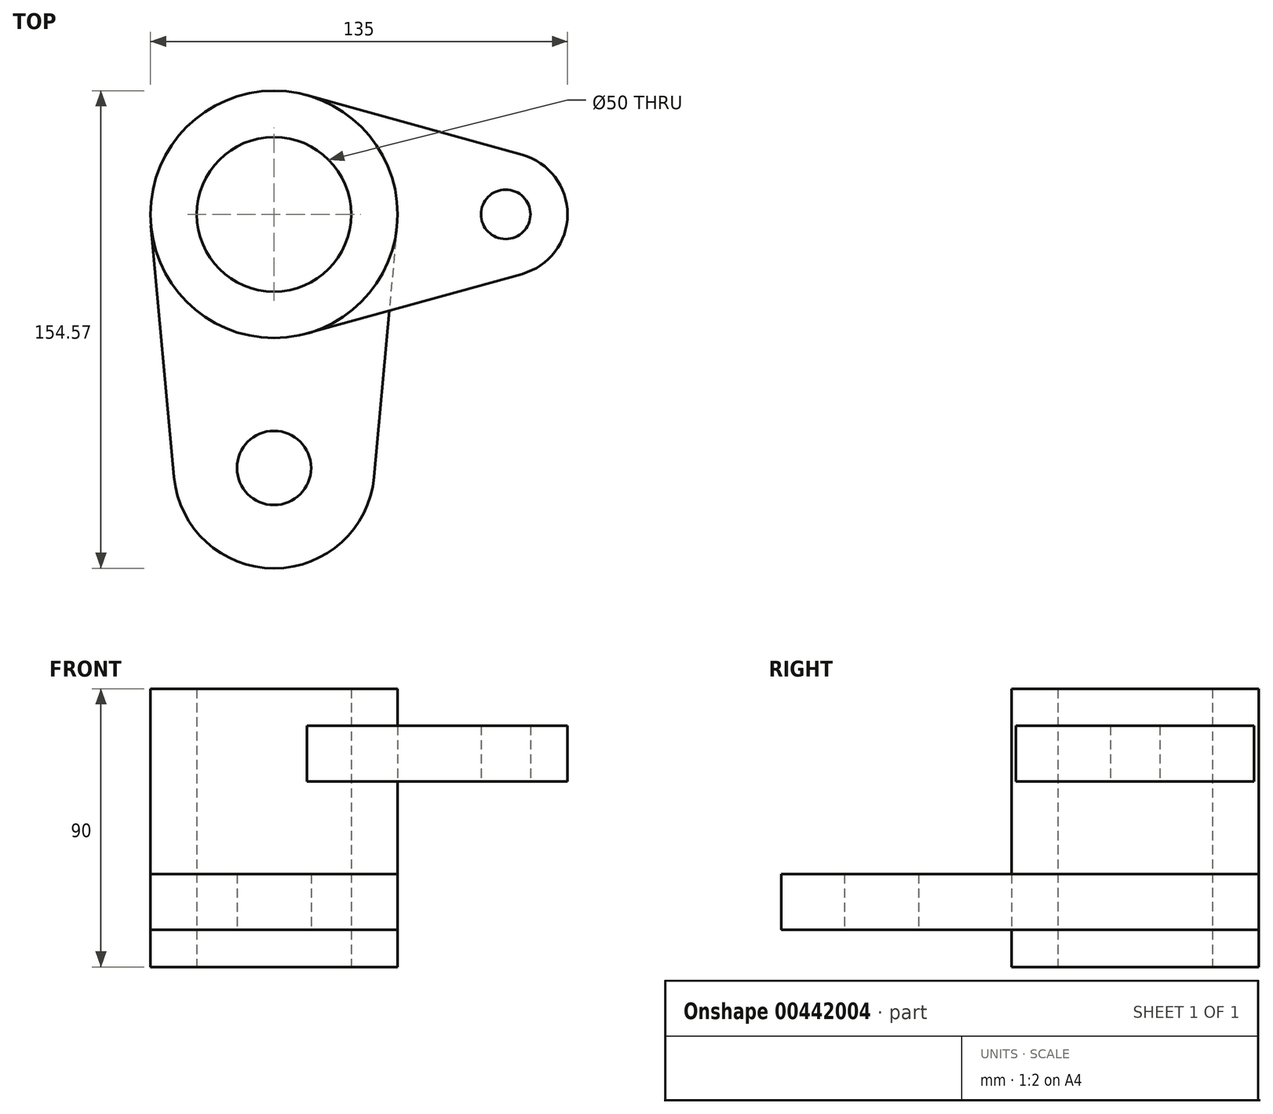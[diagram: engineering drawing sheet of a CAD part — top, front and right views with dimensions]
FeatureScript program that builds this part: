
annotation { "Feature Type Name" : "Feature", "Feature Type Description" : "" }
export const myFeature = defineFeature(function(context is Context, id is Id, definition is map)
    precondition{}
    {
        {
            var Q0;
            Q0=qCreatedBy(makeId("Top.planeOp"),FACE);
            var sketch = newSketch(context, id + "F0", { "sketchPlane" : qUnion([Q0])});
            skCircle(sketch, "E0", {"center": v(0, 0) * mm, "radius": 40 * mm});
            skCircle(sketch, "E1", {"center": v(0, 0) * mm, "radius": 25 * mm});
            skSolve(sketch);
        }
        {
            var Q0;
            Q0 = qSketchRegion(id + "F0", true);
            extrude(context, id + "F1", {"entities" : qUnion([Q0]), "depth" : 90 * mm});
        }
        {
            var Q0;
            Q0=qCreatedBy(makeId("Top.planeOp"),FACE);
            var sketch = newSketch(context, id + "F2", { "sketchPlane" : qUnion([Q0])});
            skArc(sketch, "E2", {"start": v(80.33, -19.28) * mm, "mid": v(95, 0) * mm, "end": v(80.33, 19.28) * mm});
            skLineSegment(sketch, "E3", {"start": v(10.67, 38.55) * mm, "end": v(80.33, 19.28) * mm});
            skLineSegment(sketch, "E4", {"start": v(10.67, -38.55) * mm, "end": v(80.33, -19.28) * mm});
            skLineSegment(sketch, "E5.trimOffspring", {"start": v(150, 0) * mm, "end": v(160.11, 2.8) * mm});
            skLineSegment(sketch, "E6.trimOffspring", {"start": v(150, 0) * mm, "end": v(162.18, -3.37) * mm});
            skCircle(sketch, "E7.0.0", {"center": v(0, 0) * mm, "radius": 40 * mm});
            skCircle(sketch, "E8", {"center": v(75, 0) * mm, "radius": 8 * mm});
            skSolve(sketch);
        }
        {
            var Q0;
            Q0=makeQuery(id+"F2.imprint","IMPRINT",FACE,{"disambiguationData":[TD([[makeQuery(id+"F2.imprint","IMPRINT",EDGE,{"derivedFrom":sQuery(id+"F2.wireOp",EDGE,"E2")}),1.0]])]});
            extrude(context, id + "F3", {"entities" : qUnion([Q0]), "depth" : 18 * mm});
        }
        {
            var Q0;
            Q0=makeQuery(id+"F3.opExtrude","SWEPT_BODY",BODY,{"disambiguationData":[OSD([sQuery(id+"F2.wireOp",EDGE,"E2"),sQuery(id+"F2.wireOp",EDGE,"E3"),sQuery(id+"F2.wireOp",EDGE,"E4"),sQuery(id+"F2.wireOp",EDGE,"E7.0.0"),sQuery(id+"F2.wireOp",EDGE,"E8")])]});
            transform(context, id + "F4", {"entities" : qUnion([Q0]), "transformType" : TransformType.TRANSLATION_3D, "dx" : 0 * mm, "dy" : 0 * mm, "dz" : 60 * mm, "makeCopy" : false});
        }
        {
            var Q0;
            Q0=qCreatedBy(makeId("Top.planeOp"),FACE);
            var sketch = newSketch(context, id + "F5", { "sketchPlane" : qUnion([Q0])});
            skCircle(sketch, "E9.0.0", {"center": v(0, 0) * mm, "radius": 40 * mm});
            skArc(sketch, "E10", {"start": v(-32.36, -85.04) * mm, "mid": v(0, -114.57) * mm, "end": v(32.36, -85.04) * mm});
            skLineSegment(sketch, "E11", {"start": v(-39.83, -3.66) * mm, "end": v(-32.36, -85.04) * mm});
            skLineSegment(sketch, "E12", {"start": v(39.83, -3.66) * mm, "end": v(32.36, -85.04) * mm});
            skCircle(sketch, "E13", {"center": v(0, -82.07) * mm, "radius": 12 * mm});
            skSolve(sketch);
        }
        {
            var Q0;
            Q0 = qSketchRegion(id + "F5", true);
            extrude(context, id + "F6", {"entities" : qUnion([Q0]), "depth" : 18 * mm});
        }
        {
            var Q0;
            Q0=makeQuery(id+"F6.opExtrude","SWEPT_BODY",BODY,{"disambiguationData":[OSD([sQuery(id+"F5.wireOp",EDGE,"E10"),sQuery(id+"F5.wireOp",EDGE,"E11"),sQuery(id+"F5.wireOp",EDGE,"E12"),sQuery(id+"F5.wireOp",EDGE,"E9.0.0"),sQuery(id+"F5.wireOp",EDGE,"E13")])]});
            transform(context, id + "F7", {"entities" : qUnion([Q0]), "transformType" : TransformType.TRANSLATION_3D, "dx" : 0 * mm, "dy" : 0 * mm, "dz" : 12 * mm, "makeCopy" : false});
        }
    });
